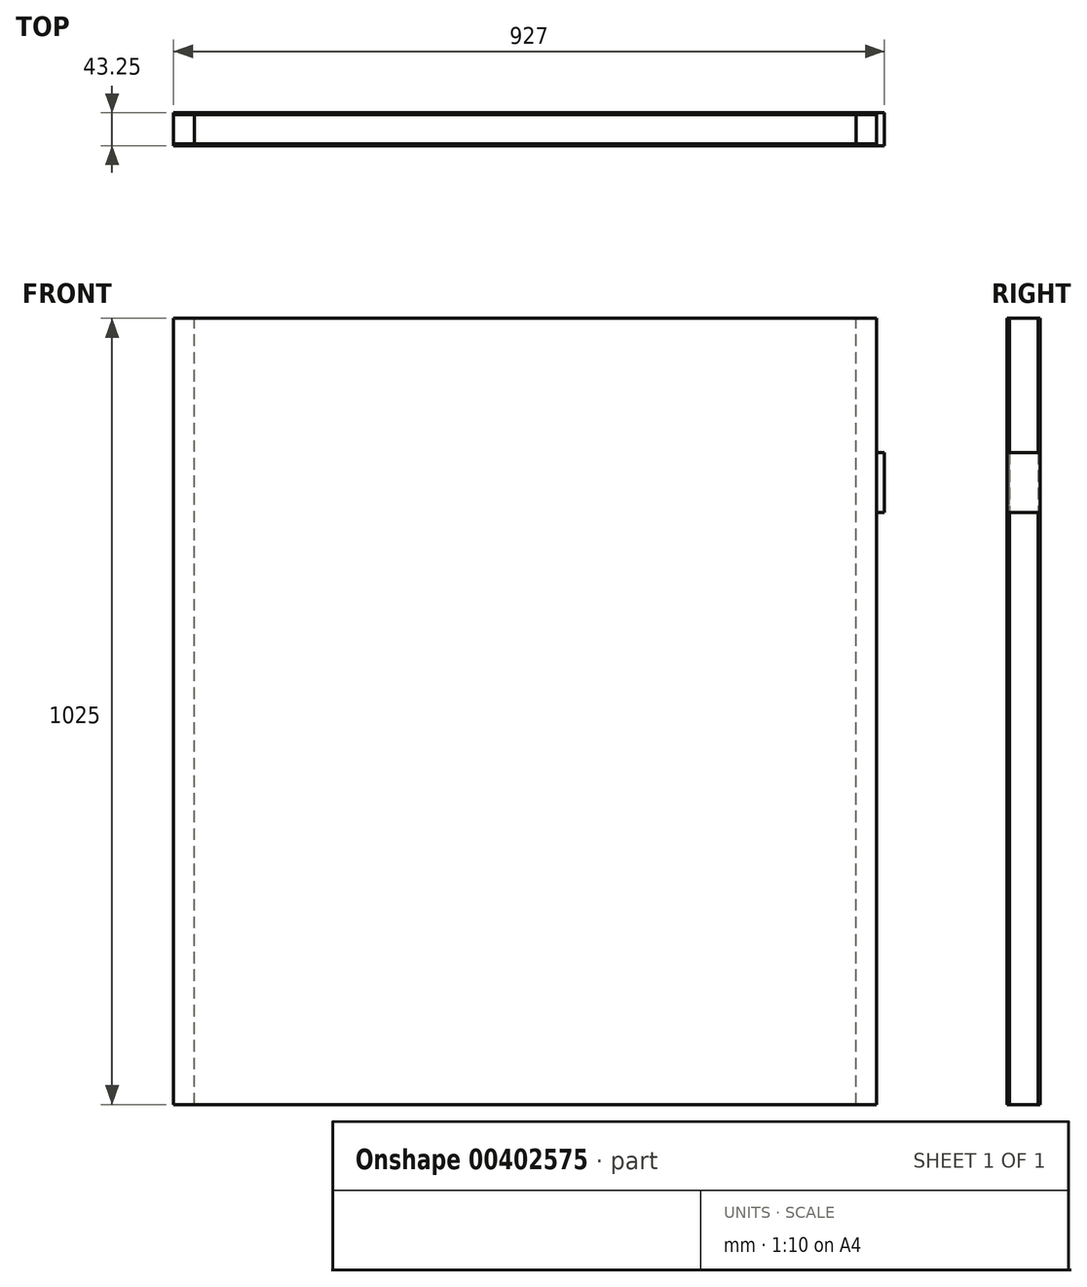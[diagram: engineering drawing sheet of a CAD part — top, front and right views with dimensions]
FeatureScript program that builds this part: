
annotation { "Feature Type Name" : "Feature", "Feature Type Description" : "" }
export const myFeature = defineFeature(function(context is Context, id is Id, definition is map)
    precondition{}
    {
        {
            var Q0;
            Q0=qCreatedBy(makeId("Front.planeOp"),FACE);
            var sketch = newSketch(context, id + "F0", { "sketchPlane" : qUnion([Q0])});
            skLineSegment(sketch, "E0.bottom", {"start": v(-458.5, 512.5) * mm, "end": v(458.5, 512.5) * mm});
            skLineSegment(sketch, "E0.top", {"start": v(-458.5, -512.5) * mm, "end": v(458.5, -512.5) * mm});
            skLineSegment(sketch, "E0.left", {"start": v(-458.5, 512.5) * mm, "end": v(-458.5, -512.5) * mm});
            skLineSegment(sketch, "E0.right", {"start": v(458.5, 512.5) * mm, "end": v(458.5, -512.5) * mm});
            skPoint(sketch, "E0.middle", {"position": v(0, 0) * mm});
            skSolve(sketch);
        }
        {
            var Q0;
            Q0=makeQuery(id+"F0.imprint","IMPRINT",FACE,{"disambiguationData":[TD([[makeQuery(id+"F0.imprint","IMPRINT",EDGE,{"derivedFrom":sQuery(id+"F0.wireOp",EDGE,"E0.bottom")}),-1.0]])]});
            extrude(context, id + "F1", {"entities" : qUnion([Q0]), "depth" : 43.25 * mm});
        }
        {
            var Q0;
            Q0=makeQuery(id+"F1.opExtrude","CAP_FACE",FACE,{"disambiguationData":[OSD([sQuery(id+"F0.wireOp",EDGE,"E0.bottom"),sQuery(id+"F0.wireOp",EDGE,"E0.top"),sQuery(id+"F0.wireOp",EDGE,"E0.left"),sQuery(id+"F0.wireOp",EDGE,"E0.right")])],"isStart":false});
            extrude(context, id + "F2", {"entities" : qUnion([Q0]), "oppositeDirection" : true, "depth" : 2.81 * mm});
        }
        {
            var Q0;
            Q0=makeQuery(id+"F1.opExtrude","CAP_FACE",FACE,{"disambiguationData":[OSD([sQuery(id+"F0.wireOp",EDGE,"E0.bottom"),sQuery(id+"F0.wireOp",EDGE,"E0.top"),sQuery(id+"F0.wireOp",EDGE,"E0.left"),sQuery(id+"F0.wireOp",EDGE,"E0.right")])],"isStart":true});
            extrude(context, id + "F3", {"entities" : qUnion([Q0]), "oppositeDirection" : true, "depth" : 2.81 * mm});
        }
        {
            var Q0;
            Q0=makeQuery(id+"F1.opExtrude","CAP_FACE",FACE,{"disambiguationData":[OSD([sQuery(id+"F0.wireOp",EDGE,"E0.bottom"),sQuery(id+"F0.wireOp",EDGE,"E0.top"),sQuery(id+"F0.wireOp",EDGE,"E0.left"),sQuery(id+"F0.wireOp",EDGE,"E0.right")])],"isStart":false});
            var sketch = newSketch(context, id + "F4", { "sketchPlane" : qUnion([Q0])});
            skLineSegment(sketch, "E1", {"start": v(458.5, 512.5) * mm, "end": v(458.5, 337.5) * mm});
            skLineSegment(sketch, "E2", {"start": v(458.5, 337.5) * mm, "end": v(468.5, 337.5) * mm});
            skLineSegment(sketch, "E3", {"start": v(468.5, 337.5) * mm, "end": v(468.5, 259.5) * mm});
            skLineSegment(sketch, "E4", {"start": v(468.5, 259.5) * mm, "end": v(458.5, 259.5) * mm});
            skLineSegment(sketch, "E5", {"start": v(458.5, 259.5) * mm, "end": v(458.5, 337.5) * mm});
            skSolve(sketch);
        }
        {
            var Q0;
            Q0=makeQuery(id+"F4.imprint","IMPRINT",FACE,{"disambiguationData":[TD([[makeQuery(id+"F4.imprint","IMPRINT",EDGE,{"derivedFrom":sQuery(id+"F4.wireOp",EDGE,"E2")}),-1.0]])]});
            extrude(context, id + "F5", {"entities" : qUnion([Q0]), "oppositeDirection" : true, "depth" : 43 * mm});
        }
        {
            var Q0;
            Q0=makeQuery(id+"F1.opExtrude","SWEPT_FACE",FACE,{"disambiguationData":[OSD([sQuery(id+"F0.wireOp",EDGE,"E0.bottom")])]});
            var sketch = newSketch(context, id + "F6", { "sketchPlane" : qUnion([Q0])});
            skLineSegment(sketch, "E6", {"start": v(458.5, -40.44) * mm, "end": v(458.5, -2.81) * mm});
            skLineSegment(sketch, "E7", {"start": v(458.5, -2.81) * mm, "end": v(431.5, -2.81) * mm});
            skLineSegment(sketch, "E8", {"start": v(431.5, -2.81) * mm, "end": v(431.5, -40.44) * mm});
            skLineSegment(sketch, "E9", {"start": v(431.5, -2.81) * mm, "end": v(458.5, -2.81) * mm});
            skLineSegment(sketch, "E10", {"start": v(431.5, -40.44) * mm, "end": v(458.5, -40.44) * mm});
            skLineSegment(sketch, "E11.2", {"start": v(-458.5, -40.44) * mm, "end": v(-458.5, -40.44) * mm});
            skLineSegment(sketch, "E12", {"start": v(-458.5, -2.81) * mm, "end": v(-458.5, -2.81) * mm});
            skLineSegment(sketch, "E13", {"start": v(-431.5, -2.81) * mm, "end": v(-431.5, -2.81) * mm});
            skLineSegment(sketch, "E14", {"start": v(-431.5, -2.81) * mm, "end": v(-431.5, -40.26) * mm});
            skLineSegment(sketch, "E15", {"start": v(-458.5, -2.81) * mm, "end": v(-431.5, -2.81) * mm});
            skLineSegment(sketch, "E16", {"start": v(-431.5, -40.26) * mm, "end": v(-431.5, -40.44) * mm});
            skLineSegment(sketch, "E17", {"start": v(-431.5, -40.26) * mm, "end": v(-458.5, -40.44) * mm});
            skLineSegment(sketch, "E18", {"start": v(-458.5, -2.81) * mm, "end": v(-458.5, -40.44) * mm});
            skSolve(sketch);
        }
        {
            var Q0;
            Q0=makeQuery(id+"F6.imprint","IMPRINT",FACE,{"disambiguationData":[TD([[makeQuery(id+"F6.imprint","IMPRINT",EDGE,{"derivedFrom":sQuery(id+"F6.wireOp",EDGE,"E14")}),-1.0]])]});
            var Q1;
            Q1=makeQuery(id+"F6.imprint","IMPRINT",FACE,{"disambiguationData":[TD([[makeQuery(id+"F6.imprint","IMPRINT",EDGE,{"derivedFrom":sQuery(id+"F6.wireOp",EDGE,"E6")}),1.0]])]});
            extrude(context, id + "F7", {"entities" : qUnion([Q0, Q1]), "endBound" : BoundingType.UP_TO_NEXT, "oppositeDirection" : true, "depth" : 25 * mm});
        }
    });
